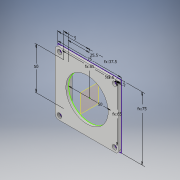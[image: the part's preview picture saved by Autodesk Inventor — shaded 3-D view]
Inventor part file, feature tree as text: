
AUTODESK INVENTOR PART (.ipt)
format: ipt  version: 2019 (Build 230136000, 136)  size: 160,256 bytes
history: native  units: mm
features: extrude x2, fillet x2, sketch x1, plane x1, mirror x1
ambient origin geometry x8: Origin, YZ Plane, XZ Plane, XY Plane, X Axis, Y Axis, Z Axis, Center Point
bodies: Solid1 (feature_tree)
feature tree (7):
  sketch  "Sketch1"  dims[d0=75.0mm d1=75.0mm d2=5.3mm d3=5.0mm d4=5.0mm d5=20.0mm d7=65.0mm d8=20.0mm d10=65.0mm d15=3.0mm d16=0.0mm d19=5.0mm d20=0.0mm d26=50.0mm d29=50.0mm d30=5.0mm d31=25.5mm d32=37.5mm d33=4.0mm d35=4.0mm]
  extrude  "Extrusion1"  Depth=75.0mm
  extrude  "Extrusion2"  Depth=4.0mm
  plane  "Work Plane1"
  mirror  "Mirror1"
  fillet  "Fillet2"  Radius=5.0mm
  fillet  "Fillet3"  Radius=5.0mm
